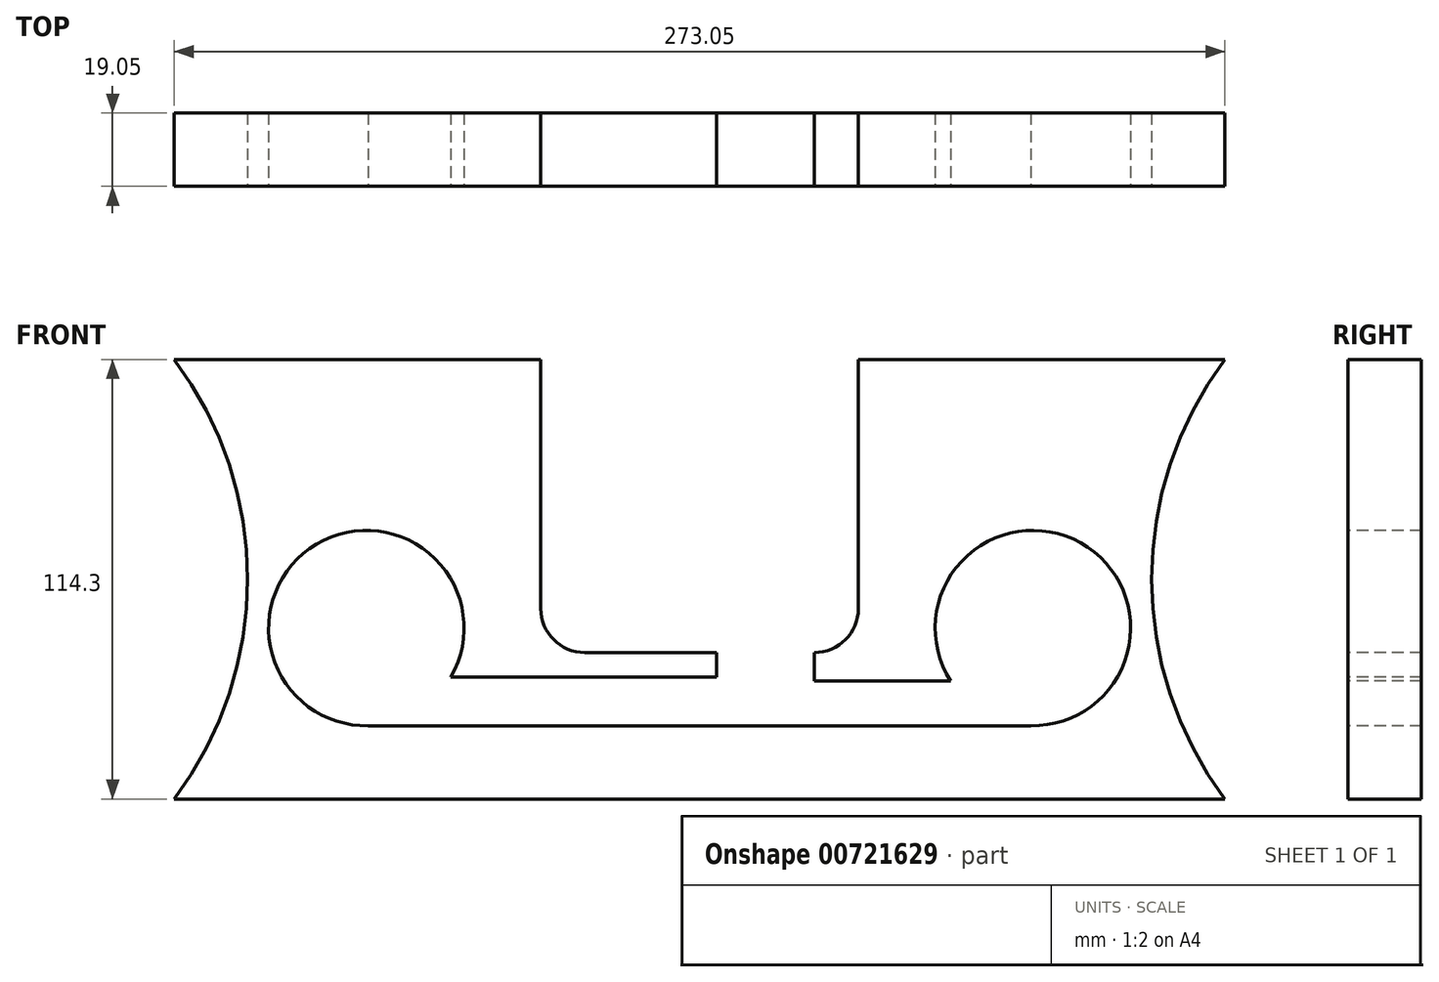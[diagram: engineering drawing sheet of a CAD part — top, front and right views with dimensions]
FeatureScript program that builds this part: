
annotation { "Feature Type Name" : "Feature", "Feature Type Description" : "" }
export const myFeature = defineFeature(function(context is Context, id is Id, definition is map)
    precondition{}
    {
        {
            var Q0;
            Q0=qCreatedBy(makeId("Front.planeOp"),FACE);
            var sketch = newSketch(context, id + "F0", { "sketchPlane" : qUnion([Q0])});
            skLineSegment(sketch, "E0.bottom", {"start": v(0, 0) * mm, "end": v(273.05, 0) * mm});
            skLineSegment(sketch, "E0.top", {"start": v(0, 114.3) * mm, "end": v(273.05, 114.3) * mm});
            skLineSegment(sketch, "E0.left", {"start": v(0, 0) * mm, "end": v(0, 114.3) * mm});
            skLineSegment(sketch, "E0.right", {"start": v(273.05, 0) * mm, "end": v(273.05, 114.3) * mm});
            skSolve(sketch);
        }
        {
            var Q0;
            Q0=makeQuery(id+"F0.imprint","IMPRINT",FACE,{"disambiguationData":[TD([[makeQuery(id+"F0.imprint","IMPRINT",EDGE,{"derivedFrom":sQuery(id+"F0.wireOp",EDGE,"E0.bottom")}),1.0]])]});
            extrude(context, id + "F1", {"entities" : qUnion([Q0]), "depth" : 19.05 * mm, "offsetDistance" : 25.4 * mm});
        }
        {
            var Q0;
            Q0=makeQuery(id+"F1.opExtrude","CAP_FACE",FACE,{"disambiguationData":[OSD([sQuery(id+"F0.wireOp",EDGE,"E0.bottom"),sQuery(id+"F0.wireOp",EDGE,"E0.top"),sQuery(id+"F0.wireOp",EDGE,"E0.left"),sQuery(id+"F0.wireOp",EDGE,"E0.right")])],"isStart":false});
            var sketch = newSketch(context, id + "F2", { "sketchPlane" : qUnion([Q0])});
            skArc(sketch, "E1", {"start": v(0, 0) * mm, "mid": v(19.05, 57.15) * mm, "end": v(0, 114.3) * mm});
            skArc(sketch, "E2", {"start": v(273.05, 114.3) * mm, "mid": v(254, 57.15) * mm, "end": v(273.05, 0) * mm});
            skSolve(sketch);
        }
        {
            var Q0;
            Q0=makeQuery(id+"F2.imprint","IMPRINT",FACE,{"disambiguationData":[TD([[makeQuery(id+"F2.imprint","IMPRINT",EDGE,{"derivedFrom":sQuery(id+"F2.wireOp",EDGE,"E1")}),1.0]])]});
            var Q1;
            Q1=makeQuery(id+"F2.imprint","IMPRINT",FACE,{"disambiguationData":[TD([[makeQuery(id+"F2.imprint","IMPRINT",EDGE,{"derivedFrom":sQuery(id+"F2.wireOp",EDGE,"E2")}),1.0]])]});
            extrude(context, id + "F3", {"entities" : qUnion([Q0, Q1]), "operationType" : NewBodyOperationType.REMOVE, "oppositeDirection" : true, "depth" : 25.4 * mm, "offsetDistance" : 25.4 * mm});
        }
        {
            var Q0;
            Q0=makeQuery(id+"F1.opExtrude","CAP_FACE",FACE,{"disambiguationData":[OSD([sQuery(id+"F0.wireOp",EDGE,"E0.bottom"),sQuery(id+"F0.wireOp",EDGE,"E0.top"),sQuery(id+"F0.wireOp",EDGE,"E0.left"),sQuery(id+"F0.wireOp",EDGE,"E0.right")])],"isStart":false});
            var sketch = newSketch(context, id + "F4", { "sketchPlane" : qUnion([Q0])});
            skLineSegment(sketch, "E3", {"start": v(95.25, 114.3) * mm, "end": v(95.25, 38.1) * mm});
            skLineSegment(sketch, "E4", {"start": v(95.25, 38.1) * mm, "end": v(177.8, 38.1) * mm});
            skLineSegment(sketch, "E5", {"start": v(177.8, 38.1) * mm, "end": v(177.8, 114.3) * mm});
            skCircle(sketch, "E6", {"center": v(49.91, 44.45) * mm, "radius": 25.4 * mm});
            skCircle(sketch, "E7", {"center": v(223.14, 44.45) * mm, "radius": 25.4 * mm});
            skCircle(sketch, "E8", {"center": v(106.68, 49.53) * mm, "radius": 11.43 * mm});
            skCircle(sketch, "E9", {"center": v(166.37, 49.53) * mm, "radius": 11.43 * mm});
            skSolve(sketch);
        }
        {
            var Q0;
            {var subQ1=makeQuery(id+"F1.opExtrude","CAP_EDGE",EDGE,{"disambiguationData":[OSD([sQuery(id+"F0.wireOp",EDGE,"E0.top")])],"isStart":false});var subQ9=sQuery(id+"F4.wireOp",EDGE,"E3");var subQ11=makeQuery(id+"F4.imprint","INTERSECT",VERTEX,{"derivedFrom":[subQ1,subQ9]});Q0=makeQuery(id+"F4.imprint","IMPRINT",FACE,{"disambiguationData":[TD([[makeQuery(id+"F4.imprint","IMPRINT",EDGE,{"disambiguationData":[TD([[subQ11,-1.0]])],"derivedFrom":subQ9}),1.0]])]});}
            var Q1;
            Q1=makeQuery(id+"F4.imprint","IMPRINT",FACE,{"disambiguationData":[TD([[makeQuery(id+"F4.imprint","IMPRINT",EDGE,{"derivedFrom":sQuery(id+"F4.wireOp",EDGE,"E6")}),1.0]])]});
            var Q2;
            Q2=makeQuery(id+"F4.imprint","IMPRINT",FACE,{"disambiguationData":[TD([[makeQuery(id+"F4.imprint","IMPRINT",EDGE,{"derivedFrom":sQuery(id+"F4.wireOp",EDGE,"E7")}),1.0]])]});
            var Q3;
            {var subQ0=sQuery(id+"F4.wireOp",EDGE,"E9");var subQ1=makeQuery(id+"F4.imprint","INTERSECT",VERTEX,{"derivedFrom":[sQuery(id+"F4.wireOp",EDGE,"E4"),subQ0]});Q3=makeQuery(id+"F4.imprint","IMPRINT",FACE,{"disambiguationData":[TD([[makeQuery(id+"F4.imprint","IMPRINT",EDGE,{"disambiguationData":[TD([[subQ1,1.0]])],"derivedFrom":subQ0}),1.0]])]});}
            var Q4;
            {var subQ0=sQuery(id+"F4.wireOp",EDGE,"E8");var subQ1=makeQuery(id+"F4.imprint","INTERSECT",VERTEX,{"derivedFrom":[sQuery(id+"F4.wireOp",EDGE,"E3"),subQ0]});Q4=makeQuery(id+"F4.imprint","IMPRINT",FACE,{"disambiguationData":[TD([[makeQuery(id+"F4.imprint","IMPRINT",EDGE,{"disambiguationData":[TD([[subQ1,-1.0]])],"derivedFrom":subQ0}),1.0]])]});}
            extrude(context, id + "F5", {"entities" : qUnion([Q0, Q1, Q2, Q3, Q4]), "operationType" : NewBodyOperationType.REMOVE, "oppositeDirection" : true, "depth" : 25.4 * mm, "offsetDistance" : 25.4 * mm});
        }
        {
            var Q0;
            Q0=makeQuery(id+"F1.opExtrude","CAP_FACE",FACE,{"disambiguationData":[OSD([sQuery(id+"F0.wireOp",EDGE,"E0.bottom"),sQuery(id+"F0.wireOp",EDGE,"E0.top"),sQuery(id+"F0.wireOp",EDGE,"E0.left"),sQuery(id+"F0.wireOp",EDGE,"E0.right")])],"isStart":false});
            var sketch = newSketch(context, id + "F6", { "sketchPlane" : qUnion([Q0])});
            skLineSegment(sketch, "E10", {"start": v(166.37, 38.1) * mm, "end": v(166.37, 30.71) * mm});
            skLineSegment(sketch, "E11", {"start": v(166.37, 30.71) * mm, "end": v(201.78, 30.71) * mm});
            skLineSegment(sketch, "E12", {"start": v(201.78, 30.71) * mm, "end": v(223.66, 19.06) * mm});
            skLineSegment(sketch, "E13", {"start": v(223.66, 19.06) * mm, "end": v(50.43, 19.06) * mm});
            skLineSegment(sketch, "E14", {"start": v(50.43, 19.06) * mm, "end": v(71.91, 31.76) * mm});
            skLineSegment(sketch, "E15", {"start": v(71.91, 31.76) * mm, "end": v(140.97, 31.76) * mm});
            skLineSegment(sketch, "E16", {"start": v(140.97, 31.76) * mm, "end": v(140.97, 38.1) * mm});
            skSolve(sketch);
        }
        {
            var Q0;
            {var subQ8=sQuery(id+"F6.wireOp",EDGE,"E10");Q0=makeQuery(id+"F6.imprint","IMPRINT",FACE,{"disambiguationData":[TD([[makeQuery(id+"F6.imprint","IMPRINT",EDGE,{"derivedFrom":subQ8}),-1.0]])]});}
            extrude(context, id + "F7", {"entities" : qUnion([Q0]), "operationType" : NewBodyOperationType.REMOVE, "oppositeDirection" : true, "depth" : 25.4 * mm, "offsetDistance" : 25.4 * mm});
        }
    });
